FCSTD DOCUMENT  (FreeCAD 0.17R13541 (Git))
Label: simple
License: All rights reserved
LicenseURL: http://en.wikipedia.org/wiki/All_rights_reserved
objects: Sketcher::SketchObject×3
note: 3 computed .brp shape members not serialized (recipe doc carries the construction recipe); baked Part::Feature solids carry a one-line shape summary decoded from their .brp

FEATURE [Sketcher::SketchObject] Sketch
  sketch-geometry (4):
    g0: LineSegment StartX=-20 StartY=10 StartZ=0 EndX=20 EndY=10 EndZ=0
    g1: LineSegment StartX=20 StartY=10 StartZ=0 EndX=20 EndY=-10 EndZ=0
    g2: LineSegment StartX=20 StartY=-10 StartZ=0 EndX=-20 EndY=-10 EndZ=0
    g3: LineSegment StartX=-20 StartY=-10 StartZ=0 EndX=-20 EndY=10 EndZ=0
  constraints (12):
    c: Coincident(g0,g1)
    c: Coincident(g1,g2)
    c: Coincident(g2,g3)
    c: Coincident(g3,g0)
    c: Horizontal(g0)
    c: Horizontal(g2)
    c: Vertical(g1)
    c: Vertical(g3)
    c: DistanceY(g-1,g0) = 10
    c: DistanceY(g2,g-1) = 10
    c: DistanceX(g2,g-1) = 20
    c: DistanceX(g-1,g1) = 20
FEATURE [Sketcher::SketchObject] Sketch001
  ExternalGeometry = -> [Sketch]
  sketch-geometry (4):
    g0: LineSegment StartX=-20 StartY=5 StartZ=0 EndX=20 EndY=5 EndZ=0
    g1: LineSegment StartX=20 StartY=5 StartZ=0 EndX=20 EndY=-5 EndZ=0
    g2: LineSegment StartX=20 StartY=-5 StartZ=0 EndX=-20 EndY=-5 EndZ=0
    g3: LineSegment StartX=-20 StartY=-5 StartZ=0 EndX=-20 EndY=5 EndZ=0
  constraints (12):
    c: Coincident(g0,g1)
    c: Coincident(g1,g2)
    c: Coincident(g2,g3)
    c: Coincident(g3,g0)
    c: Horizontal(g0)
    c: Horizontal(g2)
    c: Vertical(g1)
    c: Vertical(g3)
    c: DistanceX(g-3,g0) = 0
    c: DistanceX(g0,g-4) = 0
    c: DistanceY(g-1,g0) = 5
    c: DistanceY(g1,g-1) = 5
FEATURE [Sketcher::SketchObject] Sketch002
  sketch-geometry (8):
    g0: LineSegment StartX=-7.5 StartY=7.5 StartZ=0 EndX=7.5 EndY=7.5 EndZ=0
    g1: LineSegment StartX=7.5 StartY=7.5 StartZ=0 EndX=7.5 EndY=1 EndZ=0
    g2: LineSegment StartX=7.5 StartY=-1 StartZ=0 EndX=7.5 EndY=-7.5 EndZ=0
    g3: LineSegment StartX=7.5 StartY=-7.5 StartZ=0 EndX=-7.5 EndY=-7.5 EndZ=0
    g4: LineSegment StartX=-1 StartY=1 StartZ=0 EndX=-1 EndY=-1 EndZ=0
    g5: LineSegment StartX=-7.5 StartY=-7.5 StartZ=0 EndX=-7.5 EndY=7.5 EndZ=0
    g6: LineSegment StartX=-1 StartY=-1 StartZ=0 EndX=7.5 EndY=-1 EndZ=0
    g7: LineSegment StartX=-1 StartY=1 StartZ=0 EndX=7.5 EndY=1 EndZ=0
  constraints (24):
    c: Coincident(g0,g1)
    c: Horizontal(g0)
    c: Vertical(g1)
    c: Coincident(g2,g3)
    c: Horizontal(g3)
    c: Vertical(g2)
    c: Vertical(g4)
    c: Coincident(g5,g0)
    c: DistanceY(g3,g-1) = 7.5
    c: DistanceY(g-1,g0) = 7.5
    c: Vertical(g5)
    c: Coincident(g5,g3)
    c: DistanceX(g3,g-1) = 7.5
    c: Coincident(g6,g2)
    c: DistanceX(g-1,g2) = 7.5
    c: Horizontal(g6)
    c: Coincident(g6,g4)
    c: Coincident(g7,g4)
    c: Horizontal(g7)
    c: Coincident(g7,g1)
    c: DistanceX(g1,g2) = 0
    c: DistanceY(g-1,g4) = 1
    c: DistanceY(g4,g-1) = 1
    c: DistanceX(g4,g-1) = 1
